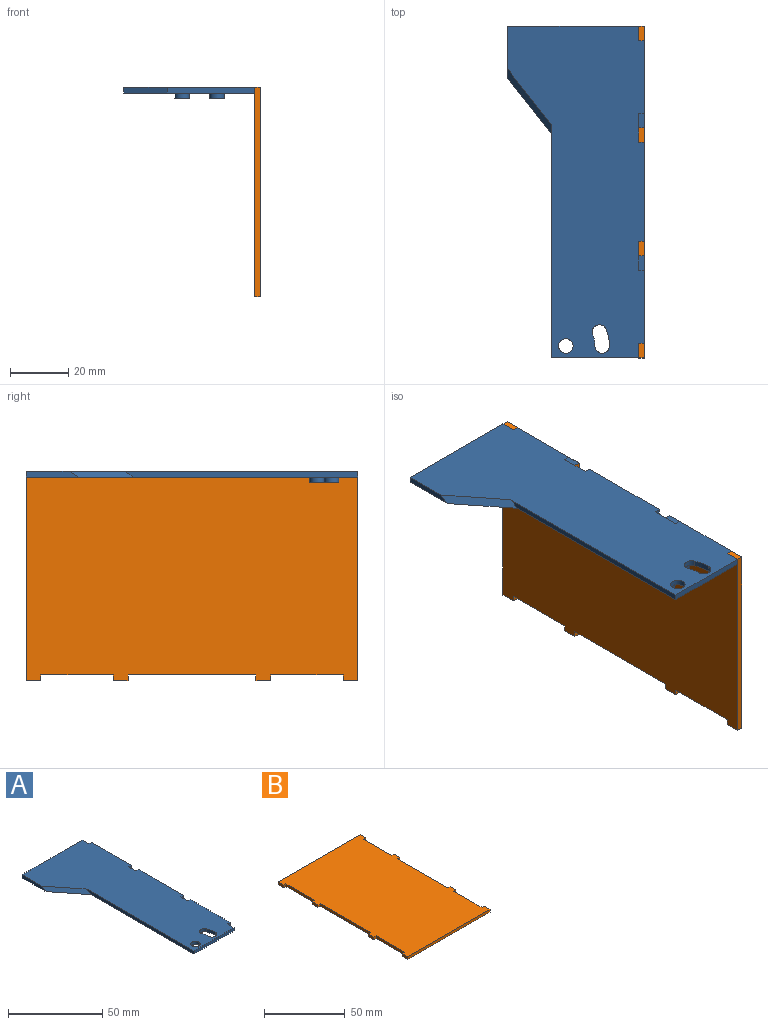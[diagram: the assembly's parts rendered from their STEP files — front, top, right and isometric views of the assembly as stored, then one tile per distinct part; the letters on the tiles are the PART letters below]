
ASSEMBLY  parts=2 mates=1
PART A: 29 faces, bbox 47x114x4 mm
  f0: plane 45x2mm, normal (0,1,0), area 90mm2, adj f4,f5,f8,f28
  f1: plane 30x2mm, normal (1,0,0), area 60mm2, adj f4,f5,f24,f27
  f2: plane 34x2mm, normal (1,0,0), area 68mm2, adj f4,f5,f22,f26
  f3: plane 30x2mm, normal (1,0,0), area 60mm2, adj f4,f5,f19,f21
  f4: plane 114x47mm, normal (0,0,1), area 3908.3mm2, adj f0,f1,f2,f3,f6,f7,f8,f13
  f5: plane 114x47mm, normal (0,0,-1), area 3917.4mm2, adj f0,f1,f2,f3,f6,f7,f8,f9
  f6: plane 80.23x2mm, normal (-1,0,0), area 157.2mm2, adj f4,f5,f7,f18
  f7: plane 30x2mm, normal (0,-1,0), area 60mm2, adj f4,f5,f6,f20
  f8: plane 18x2mm, normal (-1,0,0), area 32.8mm2, adj f0,f4,f5,f18
  f9: cylinder r=2.5mm len=5mm, axis (0,0,1), area 31.4mm2, adj f5,f10
  f10: plane 5x5mm, normal (0,0,-1), area 19.6mm2, adj f9
  f11: cylinder r=2.5mm len=5mm, axis (0,0,1), area 31.4mm2, adj f5,f12
  f12: plane 5x5mm, normal (0,0,-1), area 19.6mm2, adj f11
  f13: cylinder r=10mm len=3.83mm, axis (0,0,-1), area 7.9mm2, adj f4,f5,f14,f16
  f14: cylinder r=2.5mm len=5mm, axis (0,0,-1), area 15.7mm2, adj f4,f5,f13,f15
  f15: cylinder r=15mm len=5.74mm, axis (0,0,-1), area 11.8mm2, adj f4,f5,f14,f16
  f16: cylinder r=2.5mm len=4.81mm, axis (0,0,-1), area 15.7mm2, adj f4,f5,f13,f15
  f17: cylinder r=2.5mm len=5mm, axis (0,0,-1), area 31.4mm2, adj f4,f5
  f18: plane 22.23x15mm, normal (-0.55,-0.44,0.71), area 68.5mm2, adj f4,f5,f6,f8
  f19: plane 2x2mm, normal (0,-1,0), area 4mm2, adj f3,f4,f5,f20
  f20: plane 5x2mm, normal (1,0,0), area 10mm2, adj f4,f5,f7,f19
  f21: plane 2x2mm, normal (0,1,0), area 4mm2, adj f3,f4,f5,f23
  f22: plane 2x2mm, normal (0,-1,0), area 4mm2, adj f2,f4,f5,f23
  f23: plane 5x2mm, normal (1,0,0), area 10mm2, adj f4,f5,f21,f22
  f24: plane 2x2mm, normal (0,-1,0), area 4mm2, adj f1,f4,f5,f25
  f25: plane 5x2mm, normal (1,0,0), area 10mm2, adj f4,f5,f24,f26
  f26: plane 2x2mm, normal (0,1,0), area 4mm2, adj f2,f4,f5,f25
  f27: plane 2x2mm, normal (0,1,0), area 4mm2, adj f1,f4,f5,f28
  f28: plane 5x2mm, normal (1,0,0), area 10mm2, adj f0,f4,f5,f27
PART B: 30 faces, bbox 72x114x2 mm
  f0: plane 2x2mm, normal (0,1,0), area 4mm2, adj f1,f27,f28,f29
  f1: plane 44x2mm, normal (1,0,0), area 88mm2, adj f0,f2,f28,f29
  f2: plane 2x2mm, normal (0,-1,0), area 4mm2, adj f1,f3,f28,f29
  f3: plane 5x2mm, normal (1,0,0), area 10mm2, adj f2,f4,f28,f29
  f4: plane 2x2mm, normal (0,1,0), area 4mm2, adj f3,f5,f28,f29
  f5: plane 25x2mm, normal (1,0,0), area 50mm2, adj f4,f6,f28,f29
  f6: plane 2x2mm, normal (0,-1,0), area 4mm2, adj f5,f7,f28,f29
  f7: plane 5x2mm, normal (1,0,0), area 10mm2, adj f6,f8,f28,f29
  f8: plane 72x2mm, normal (0,1,0), area 144mm2, adj f7,f9,f28,f29
  f9: plane 5x2mm, normal (-1,0,0), area 10mm2, adj f8,f10,f28,f29
  f10: plane 2x2mm, normal (0,-1,0), area 4mm2, adj f9,f11,f28,f29
  f11: plane 25x2mm, normal (-1,0,0), area 50mm2, adj f10,f12,f28,f29
  f12: plane 2x2mm, normal (0,1,0), area 4mm2, adj f11,f13,f28,f29
  f13: plane 5x2mm, normal (-1,0,0), area 10mm2, adj f12,f14,f28,f29
  f14: plane 2x2mm, normal (0,-1,0), area 4mm2, adj f13,f15,f28,f29
  f15: plane 44x2mm, normal (-1,0,0), area 88mm2, adj f14,f16,f28,f29
  f16: plane 2x2mm, normal (0,1,0), area 4mm2, adj f15,f17,f28,f29
  f17: plane 5x2mm, normal (-1,0,0), area 10mm2, adj f16,f18,f28,f29
  f18: plane 2x2mm, normal (0,-1,0), area 4mm2, adj f17,f19,f28,f29
  f19: plane 25x2mm, normal (-1,0,0), area 50mm2, adj f18,f20,f28,f29
  f20: plane 2x2mm, normal (0,1,0), area 4mm2, adj f19,f21,f28,f29
  f21: plane 5x2mm, normal (-1,0,0), area 10mm2, adj f20,f22,f28,f29
  f22: plane 72x2mm, normal (0,-1,0), area 144mm2, adj f21,f23,f28,f29
  f23: plane 5x2mm, normal (1,0,0), area 10mm2, adj f22,f24,f28,f29
  f24: plane 2x2mm, normal (0,1,0), area 4mm2, adj f23,f25,f28,f29
  f25: plane 25x2mm, normal (1,0,0), area 50mm2, adj f24,f26,f28,f29
  f26: plane 2x2mm, normal (0,-1,0), area 4mm2, adj f25,f27,f28,f29
  f27: plane 5x2mm, normal (1,0,0), area 10mm2, adj f0,f26,f28,f29
  f28: plane 114x72mm, normal (0,0,1), area 7832mm2, adj f0,f1,f2,f3,f4,f5,f6,f7
  f29: plane 114x72mm, normal (0,0,-1), area 7832mm2, adj f0,f1,f2,f3,f4,f5,f6,f7
PLACE A t=(-8.56,-53.79,0)mm
PLACE B rot(axis=(0,1,0),90deg) t=(16.44,-12,-35.18)mm
MATE fastened B.f29 <-> A.f28  axis (-1,0,0) through (16.44,48.71,2)mm
